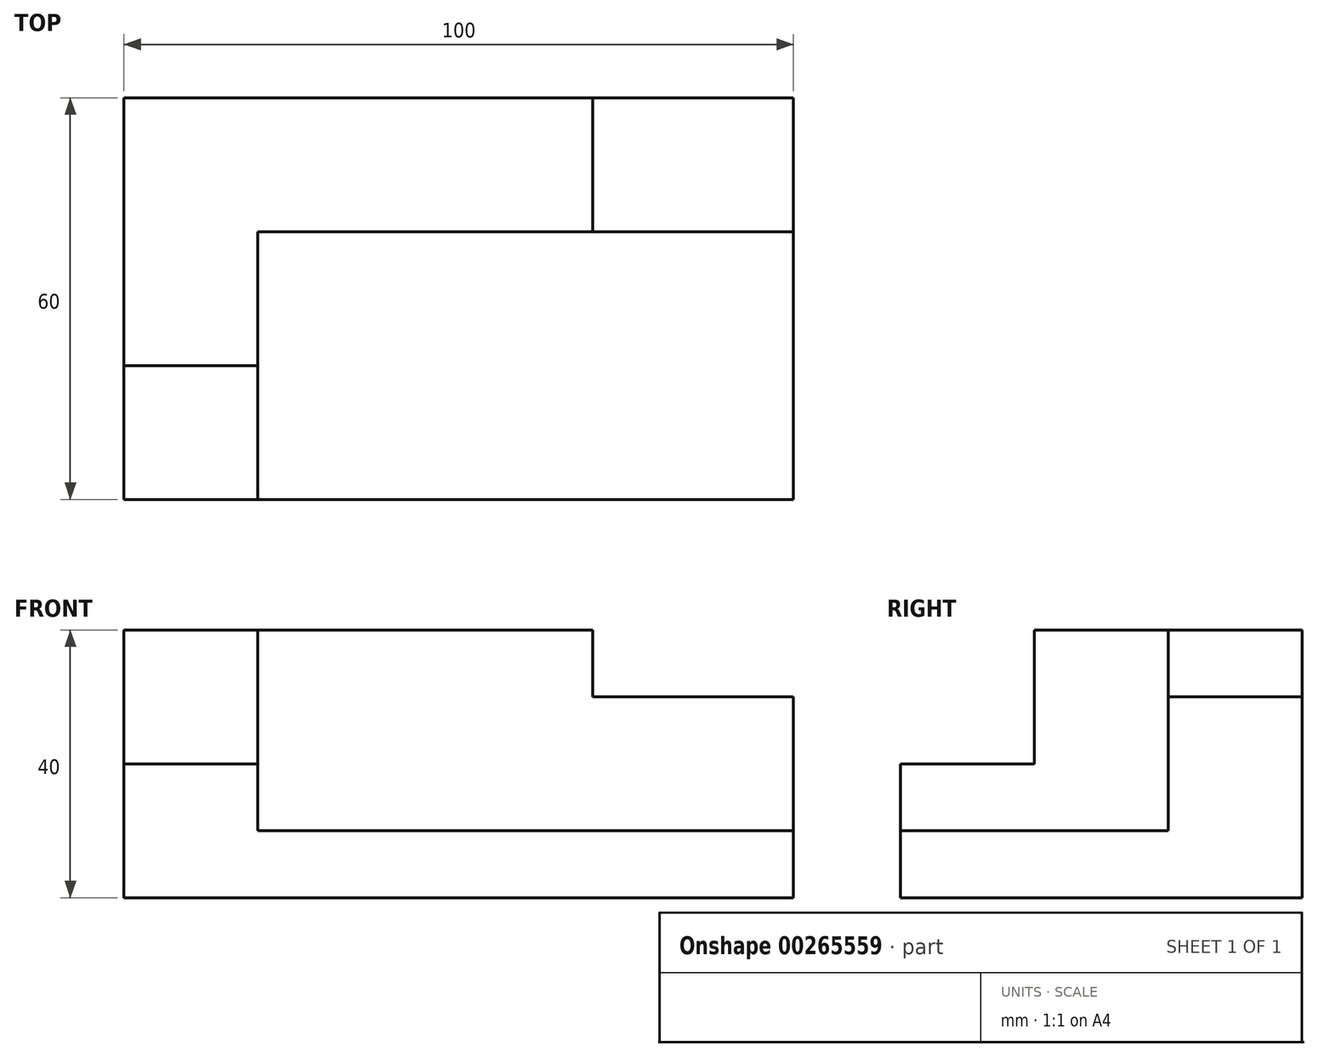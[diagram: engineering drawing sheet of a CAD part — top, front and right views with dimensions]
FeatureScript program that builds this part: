
annotation { "Feature Type Name" : "Feature", "Feature Type Description" : "" }
export const myFeature = defineFeature(function(context is Context, id is Id, definition is map)
    precondition{}
    {
        {
            var Q0;
            Q0=qCreatedBy(makeId("Top.planeOp"),FACE);
            var sketch = newSketch(context, id + "F0", { "sketchPlane" : qUnion([Q0])});
            skLineSegment(sketch, "E0.bottom", {"start": v(-50, 30) * mm, "end": v(50, 30) * mm});
            skLineSegment(sketch, "E0.top", {"start": v(-50, -30) * mm, "end": v(50, -30) * mm});
            skLineSegment(sketch, "E0.left", {"start": v(-50, 30) * mm, "end": v(-50, -30) * mm});
            skLineSegment(sketch, "E0.right", {"start": v(50, 30) * mm, "end": v(50, -30) * mm});
            skPoint(sketch, "E0.middle", {"position": v(0, 0) * mm});
            skSolve(sketch);
        }
        {
            var Q0;
            Q0 = qSketchRegion(id + "F0", true);
            extrude(context, id + "F1", {"entities" : qUnion([Q0]), "depth" : 40 * mm});
        }
        {
            var Q0;
            Q0=makeQuery(id+"F1.opExtrude","CAP_FACE",FACE,{"disambiguationData":[OSD([sQuery(id+"F0.wireOp",EDGE,"E0.bottom"),sQuery(id+"F0.wireOp",EDGE,"E0.top"),sQuery(id+"F0.wireOp",EDGE,"E0.left"),sQuery(id+"F0.wireOp",EDGE,"E0.right")])],"isStart":false});
            var sketch = newSketch(context, id + "F2", { "sketchPlane" : qUnion([Q0])});
            skLineSegment(sketch, "E1.bottom", {"start": v(50, -30) * mm, "end": v(-30, -30) * mm});
            skLineSegment(sketch, "E1.top", {"start": v(50, 10) * mm, "end": v(-30, 10) * mm});
            skLineSegment(sketch, "E1.left", {"start": v(50, -30) * mm, "end": v(50, 10) * mm});
            skLineSegment(sketch, "E1.right", {"start": v(-30, -30) * mm, "end": v(-30, 10) * mm});
            skSolve(sketch);
        }
        {
            var Q0;
            Q0 = qSketchRegion(id + "F2", true);
            extrude(context, id + "F3", {"entities" : qUnion([Q0]), "operationType" : NewBodyOperationType.REMOVE, "oppositeDirection" : true, "depth" : 30 * mm});
        }
        {
            var Q0;
            Q0=makeQuery(id+"F3.boolean.opBoolean","COPY",FACE,{"derivedFrom":makeQuery(id+"F3.opExtrude","SWEPT_FACE",FACE,{"disambiguationData":[OSD([sQuery(id+"F2.wireOp",EDGE,"E1.top")])]})});
            var sketch = newSketch(context, id + "F4", { "sketchPlane" : qUnion([Q0])});
            skLineSegment(sketch, "E2.bottom", {"start": v(50, 40) * mm, "end": v(20, 40) * mm});
            skLineSegment(sketch, "E2.top", {"start": v(50, 30) * mm, "end": v(20, 30) * mm});
            skLineSegment(sketch, "E2.left", {"start": v(50, 40) * mm, "end": v(50, 30) * mm});
            skLineSegment(sketch, "E2.right", {"start": v(20, 40) * mm, "end": v(20, 30) * mm});
            skSolve(sketch);
        }
        {
            var Q0;
            Q0 = qSketchRegion(id + "F4", true);
            extrude(context, id + "F5", {"entities" : qUnion([Q0]), "operationType" : NewBodyOperationType.REMOVE, "endBound" : BoundingType.THROUGH_ALL, "oppositeDirection" : true, "depth" : 25 * mm});
        }
        {
            var Q0;
            Q0=makeQuery(id+"F3.boolean.opBoolean","COPY",FACE,{"derivedFrom":makeQuery(id+"F3.opExtrude","SWEPT_FACE",FACE,{"disambiguationData":[OSD([sQuery(id+"F2.wireOp",EDGE,"E1.right")])]})});
            var sketch = newSketch(context, id + "F6", { "sketchPlane" : qUnion([Q0])});
            skLineSegment(sketch, "E3.bottom", {"start": v(-30, 40) * mm, "end": v(-10, 40) * mm});
            skLineSegment(sketch, "E3.top", {"start": v(-30, 20) * mm, "end": v(-10, 20) * mm});
            skLineSegment(sketch, "E3.left", {"start": v(-30, 40) * mm, "end": v(-30, 20) * mm});
            skLineSegment(sketch, "E3.right", {"start": v(-10, 40) * mm, "end": v(-10, 20) * mm});
            skSolve(sketch);
        }
        {
            var Q0;
            Q0 = qSketchRegion(id + "F6", true);
            extrude(context, id + "F7", {"entities" : qUnion([Q0]), "operationType" : NewBodyOperationType.REMOVE, "endBound" : BoundingType.THROUGH_ALL, "oppositeDirection" : true, "depth" : 25 * mm});
        }
    });
